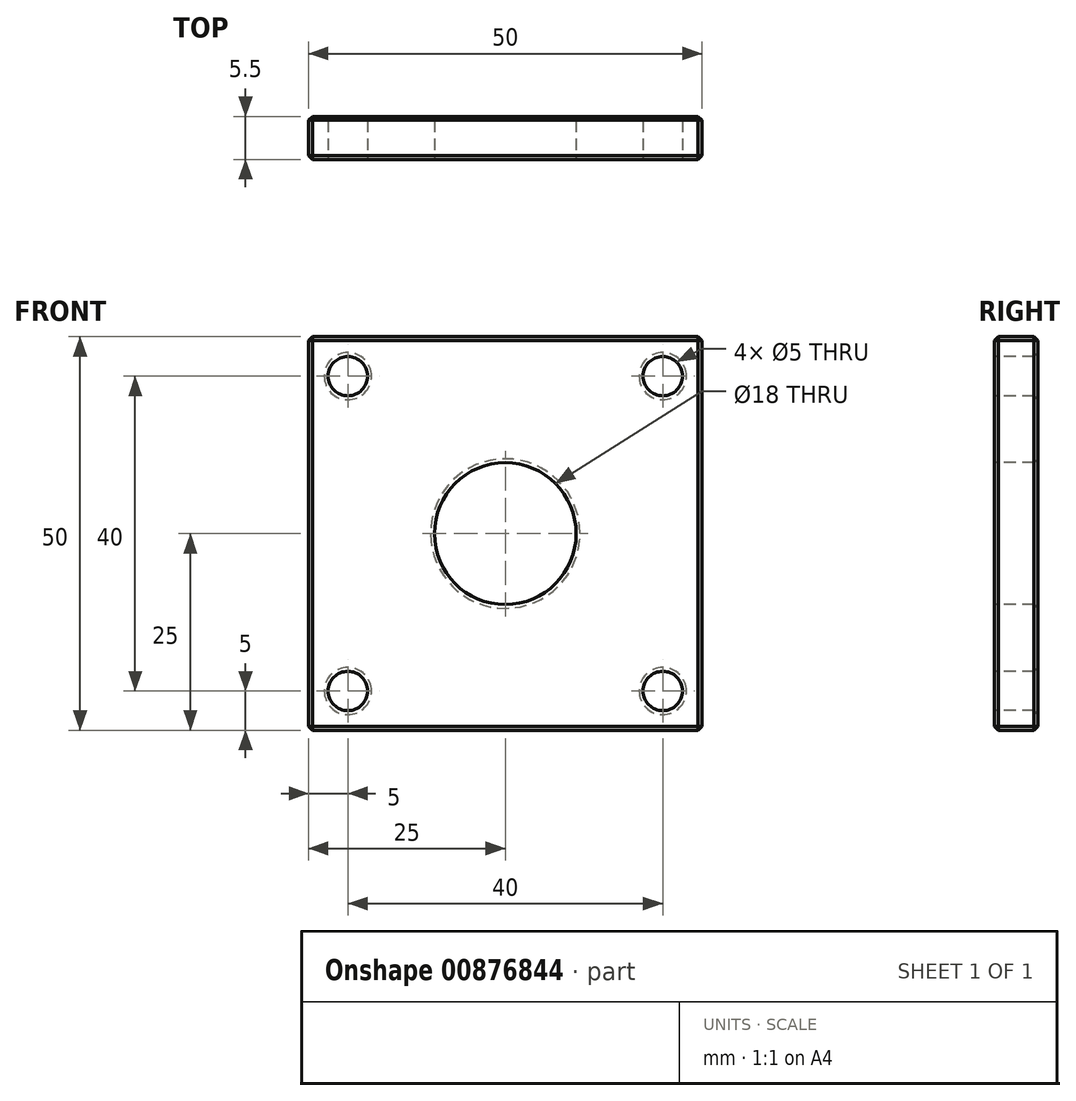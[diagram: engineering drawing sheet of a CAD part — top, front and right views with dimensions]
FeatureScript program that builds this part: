
annotation { "Feature Type Name" : "Feature", "Feature Type Description" : "" }
export const myFeature = defineFeature(function(context is Context, id is Id, definition is map)
    precondition{}
    {
        {
            var Q0;
            Q0=qCreatedBy(makeId("Front.planeOp"),FACE);
            var sketch = newSketch(context, id + "F0", { "sketchPlane" : qUnion([Q0])});
            skLineSegment(sketch, "E0.bottom", {"start": v(25, -25) * mm, "end": v(-25, -25) * mm});
            skLineSegment(sketch, "E0.top", {"start": v(25, 25) * mm, "end": v(-25, 25) * mm});
            skLineSegment(sketch, "E0.left", {"start": v(25, -25) * mm, "end": v(25, 25) * mm});
            skLineSegment(sketch, "E0.right", {"start": v(-25, -25) * mm, "end": v(-25, 25) * mm});
            skPoint(sketch, "E0.middle", {"position": v(0, 0) * mm});
            skSolve(sketch);
        }
        {
            var Q0;
            Q0 = qSketchRegion(id + "F0", true);
            extrude(context, id + "F1", {"entities" : qUnion([Q0]), "oppositeDirection" : true, "depth" : 5.5 * mm, "offsetDistance" : 25 * mm});
        }
        {
            var Q0;
            Q0=makeQuery(id+"F1.opExtrude","CAP_FACE",FACE,{"disambiguationData":[OSD([sQuery(id+"F0.wireOp",EDGE,"E0.bottom"),sQuery(id+"F0.wireOp",EDGE,"E0.top"),sQuery(id+"F0.wireOp",EDGE,"E0.left"),sQuery(id+"F0.wireOp",EDGE,"E0.right")])],"isStart":true});
            var sketch = newSketch(context, id + "F2", { "sketchPlane" : qUnion([Q0])});
            skCircle(sketch, "E1", {"center": v(0, 0) * mm, "radius": 9 * mm});
            skSolve(sketch);
        }
        {
            var Q0;
            Q0 = qSketchRegion(id + "F2", true);
            extrude(context, id + "F3", {"entities" : qUnion([Q0]), "operationType" : NewBodyOperationType.REMOVE, "oppositeDirection" : true, "depth" : 25 * mm, "offsetDistance" : 25 * mm});
        }
        {
            var Q0;
            Q0=makeQuery(id+"F1.opExtrude","CAP_FACE",FACE,{"disambiguationData":[OSD([sQuery(id+"F0.wireOp",EDGE,"E0.bottom"),sQuery(id+"F0.wireOp",EDGE,"E0.top"),sQuery(id+"F0.wireOp",EDGE,"E0.left"),sQuery(id+"F0.wireOp",EDGE,"E0.right")])],"isStart":true});
            var sketch = newSketch(context, id + "F4", { "sketchPlane" : qUnion([Q0])});
            skLineSegment(sketch, "E2", {"start": v(-20, 25) * mm, "end": v(-20, 13.74) * mm, "construction": true});
            skLineSegment(sketch, "E3", {"start": v(-25, 20) * mm, "end": v(-15.71, 20) * mm, "construction": true});
            skLineSegment(sketch, "E4", {"start": v(20, 25) * mm, "end": v(20, 13.21) * mm, "construction": true});
            skLineSegment(sketch, "E5", {"start": v(25, 20) * mm, "end": v(13.87, 20) * mm, "construction": true});
            skLineSegment(sketch, "E6", {"start": v(-25, -20) * mm, "end": v(-14.8, -20) * mm, "construction": true});
            skLineSegment(sketch, "E7", {"start": v(-20, -15.83) * mm, "end": v(-20, -25) * mm, "construction": true});
            skLineSegment(sketch, "E8", {"start": v(25, -20) * mm, "end": v(11.84, -20) * mm, "construction": true});
            skLineSegment(sketch, "E9", {"start": v(20, -12.6) * mm, "end": v(20, -25) * mm, "construction": true});
            skCircle(sketch, "E10", {"center": v(-20, -20) * mm, "radius": 2.5 * mm});
            skCircle(sketch, "E11", {"center": v(20, -20) * mm, "radius": 2.5 * mm});
            skCircle(sketch, "E12", {"center": v(-20, 20) * mm, "radius": 2.5 * mm});
            skCircle(sketch, "E13", {"center": v(20, 20) * mm, "radius": 2.5 * mm});
            skSolve(sketch);
        }
        {
            var Q0;
            Q0 = qSketchRegion(id + "F4", true);
            extrude(context, id + "F5", {"entities" : qUnion([Q0]), "operationType" : NewBodyOperationType.REMOVE, "oppositeDirection" : true, "depth" : 25 * mm, "offsetDistance" : 25 * mm});
        }
        {
            var Q0;
            Q0=makeQuery(id+"F1.opExtrude","CAP_EDGE",EDGE,{"disambiguationData":[OSD([sQuery(id+"F0.wireOp",EDGE,"E0.bottom")])],"isStart":true});
            var Q1;
            Q1=makeQuery(id+"F1.opExtrude","CAP_EDGE",EDGE,{"disambiguationData":[OSD([sQuery(id+"F0.wireOp",EDGE,"E0.right")])],"isStart":true});
            var Q2;
            Q2=makeQuery(id+"F1.opExtrude","CAP_EDGE",EDGE,{"disambiguationData":[OSD([sQuery(id+"F0.wireOp",EDGE,"E0.top")])],"isStart":true});
            var Q3;
            Q3=makeQuery(id+"F1.opExtrude","CAP_EDGE",EDGE,{"disambiguationData":[OSD([sQuery(id+"F0.wireOp",EDGE,"E0.left")])],"isStart":true});
            var Q4;
            Q4=makeQuery(id+"F1.opExtrude","SWEPT_EDGE",EDGE,{"disambiguationData":[OSD([sQuery(id+"F0.wireOp",EDGE,"E0.bottom"),sQuery(id+"F0.wireOp",EDGE,"E0.left")])]});
            var Q5;
            Q5=makeQuery(id+"F1.opExtrude","SWEPT_EDGE",EDGE,{"disambiguationData":[OSD([sQuery(id+"F0.wireOp",EDGE,"E0.bottom"),sQuery(id+"F0.wireOp",EDGE,"E0.right")])]});
            var Q6;
            Q6=makeQuery(id+"F1.opExtrude","SWEPT_EDGE",EDGE,{"disambiguationData":[OSD([sQuery(id+"F0.wireOp",EDGE,"E0.top"),sQuery(id+"F0.wireOp",EDGE,"E0.right")])]});
            var Q7;
            Q7=makeQuery(id+"F1.opExtrude","SWEPT_EDGE",EDGE,{"disambiguationData":[OSD([sQuery(id+"F0.wireOp",EDGE,"E0.top"),sQuery(id+"F0.wireOp",EDGE,"E0.left")])]});
            var Q8;
            Q8=makeQuery(id+"F1.opExtrude","CAP_EDGE",EDGE,{"disambiguationData":[OSD([sQuery(id+"F0.wireOp",EDGE,"E0.top")])],"isStart":false});
            var Q9;
            Q9=makeQuery(id+"F1.opExtrude","CAP_EDGE",EDGE,{"disambiguationData":[OSD([sQuery(id+"F0.wireOp",EDGE,"E0.left")])],"isStart":false});
            var Q10;
            Q10=makeQuery(id+"F1.opExtrude","CAP_EDGE",EDGE,{"disambiguationData":[OSD([sQuery(id+"F0.wireOp",EDGE,"E0.bottom")])],"isStart":false});
            var Q11;
            Q11=makeQuery(id+"F1.opExtrude","CAP_FACE",FACE,{"disambiguationData":[OSD([sQuery(id+"F0.wireOp",EDGE,"E0.bottom"),sQuery(id+"F0.wireOp",EDGE,"E0.top"),sQuery(id+"F0.wireOp",EDGE,"E0.left"),sQuery(id+"F0.wireOp",EDGE,"E0.right")])],"isStart":false});
            chamfer(context, id + "F6", {"entities" : qUnion([Q0, Q1, Q2, Q3, Q4, Q5, Q6, Q7, Q8, Q9, Q10, Q11]), "width" : 0.5 * mm, "tangentPropagation" : true});
        }
    });
